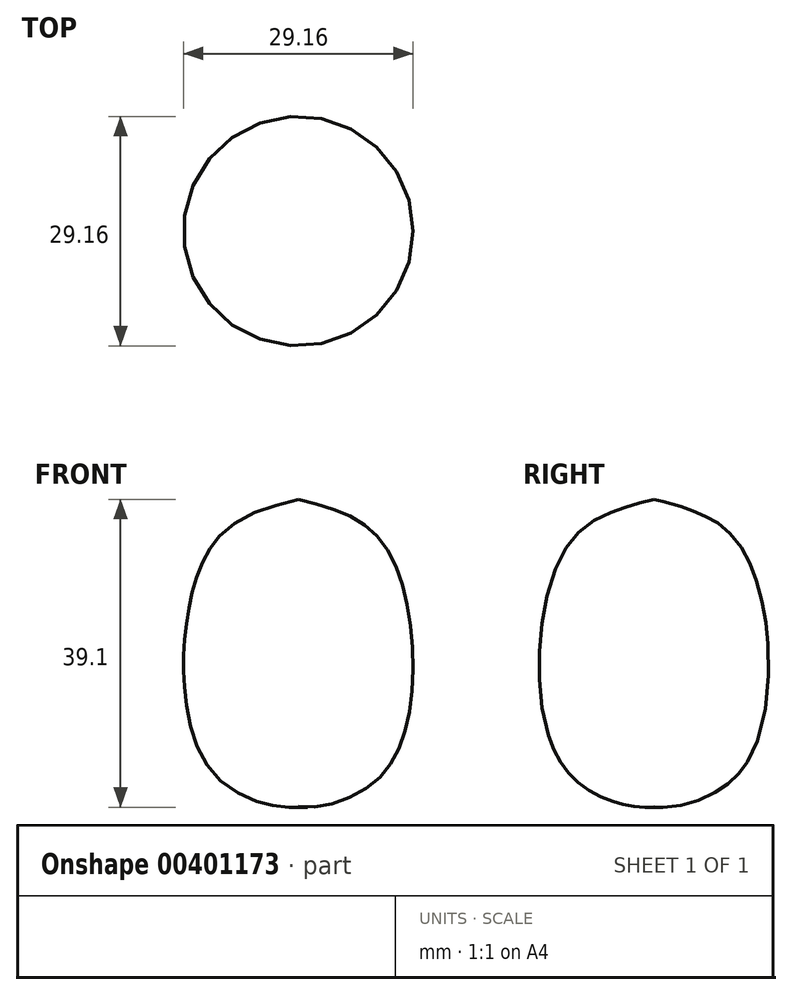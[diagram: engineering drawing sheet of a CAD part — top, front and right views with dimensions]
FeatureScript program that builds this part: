
annotation { "Feature Type Name" : "Feature", "Feature Type Description" : "" }
export const myFeature = defineFeature(function(context is Context, id is Id, definition is map)
    precondition{}
    {
        {
            var Q0;
            Q0=qCreatedBy(makeId("Front.planeOp"),FACE);
            var sketch = newSketch(context, id + "F0", { "sketchPlane" : qUnion([Q0])});
            skLineSegment(sketch, "E0", {"start": v(0, 74.1) * mm, "end": v(0, 0) * mm});
            skFitSpline(sketch, "E1", {"points": [v(0, 46.5) * mm, v(9.07, 42.76) * mm, v(13.8, 33.3) * mm, v(14, 18.92) * mm, v(9.26, 10.25) * mm, v(0, 7.49) * mm], "startDerivative": vector(52.61, -13.4) * mm, "endDerivative": vector(-43.74, 6.25) * mm});
            skSolve(sketch);
        }
        {
            var Q0;
            {var subQ0=sQuery(id+"F0.wireOp",EDGE,"E1");Q0=makeQuery(id+"F0.imprint","IMPRINT",FACE,{"disambiguationData":[TD([[makeQuery(id+"F0.imprint","IMPRINT",EDGE,{"derivedFrom":subQ0}),-1.0]])]});}
            var Q1;
            Q1=sQuery(id+"F0.wireOp",EDGE,"E0");
            revolve(context, id + "F1", {"entities" : qUnion([Q0]), "axis" : qUnion([Q1]), "revolveType" : RevolveType.FULL});
        }
    });
